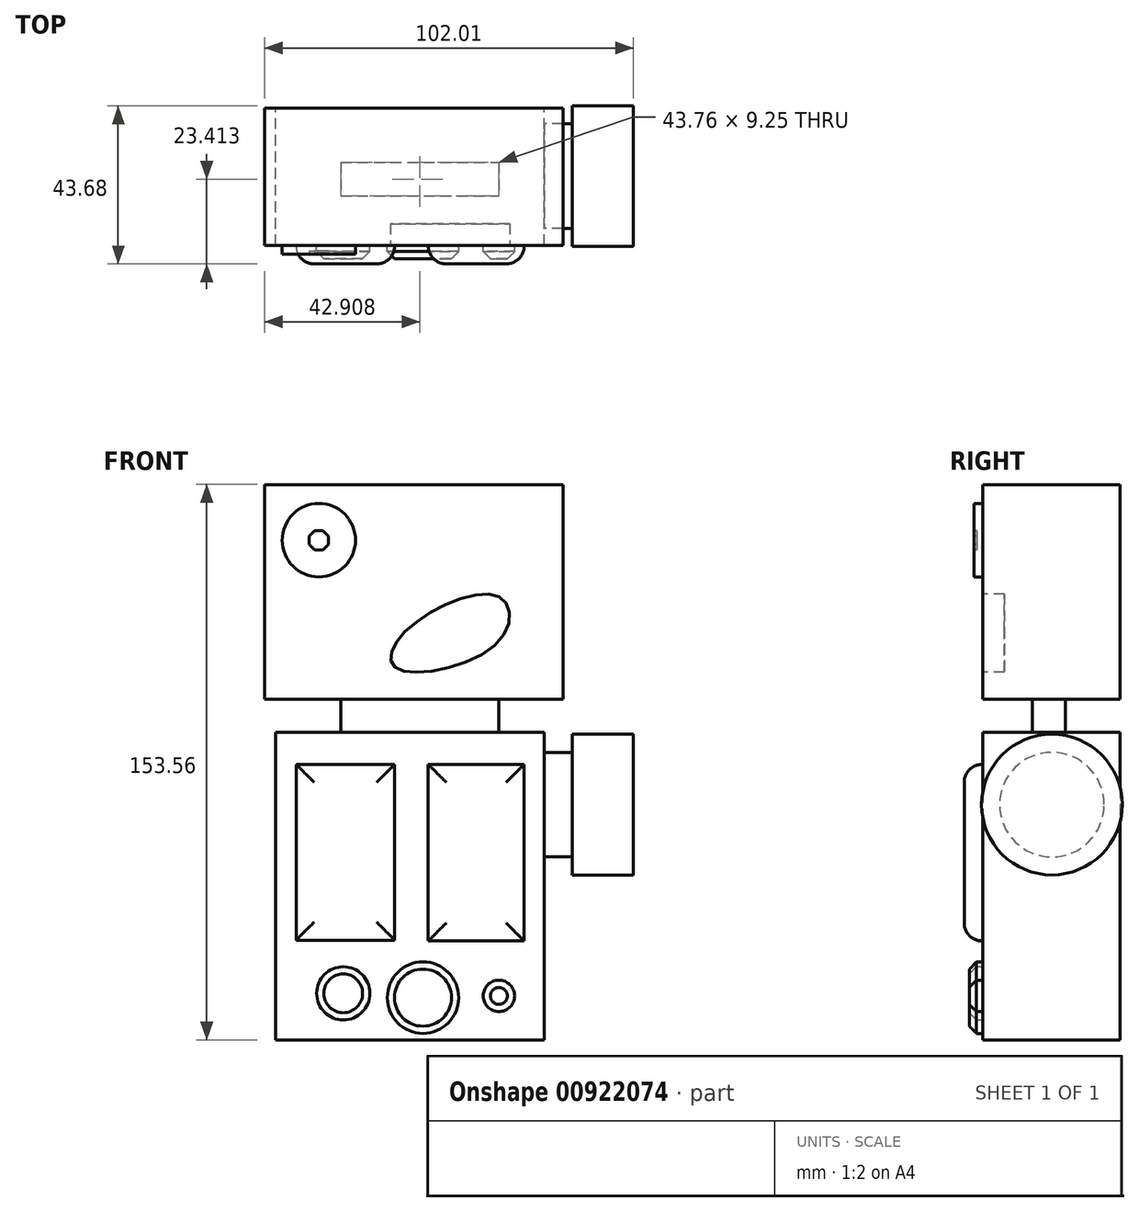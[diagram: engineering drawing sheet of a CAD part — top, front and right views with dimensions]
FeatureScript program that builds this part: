
annotation { "Feature Type Name" : "Feature", "Feature Type Description" : "" }
export const myFeature = defineFeature(function(context is Context, id is Id, definition is map)
    precondition{}
    {
        {
            var Q0;
            Q0=qCreatedBy(makeId("Front.planeOp"),FACE);
            var sketch = newSketch(context, id + "F0", { "sketchPlane" : qUnion([Q0])});
            skLineSegment(sketch, "E0.bottom", {"start": v(-61.73, 38.4) * mm, "end": v(12.52, 38.4) * mm});
            skLineSegment(sketch, "E0.top", {"start": v(-61.73, -46.66) * mm, "end": v(12.52, -46.66) * mm});
            skLineSegment(sketch, "E0.left", {"start": v(-61.73, 38.4) * mm, "end": v(-61.73, -46.66) * mm});
            skLineSegment(sketch, "E0.right", {"start": v(12.52, 38.4) * mm, "end": v(12.52, -46.66) * mm});
            skSolve(sketch);
        }
        {
            var Q0;
            Q0 = qSketchRegion(id + "F0", true);
            extrude(context, id + "F1", {"entities" : qUnion([Q0]), "depth" : 38 * mm, "offsetDistance" : 25 * mm});
        }
        {
            var Q0;
            Q0=makeQuery(id+"F1.opExtrude","CAP_FACE",FACE,{"disambiguationData":[OSD([sQuery(id+"F0.wireOp",EDGE,"E0.bottom"),sQuery(id+"F0.wireOp",EDGE,"E0.top"),sQuery(id+"F0.wireOp",EDGE,"E0.left"),sQuery(id+"F0.wireOp",EDGE,"E0.right")])],"isStart":false});
            var sketch = newSketch(context, id + "F2", { "sketchPlane" : qUnion([Q0])});
            skLineSegment(sketch, "E1.bottom", {"start": v(-56.1, 29.53) * mm, "end": v(-28.82, 29.53) * mm});
            skLineSegment(sketch, "E1.top", {"start": v(-56.1, -19.1) * mm, "end": v(-28.82, -19.1) * mm});
            skLineSegment(sketch, "E1.left", {"start": v(-56.1, 29.53) * mm, "end": v(-56.1, -19.1) * mm});
            skLineSegment(sketch, "E1.right", {"start": v(-28.82, 29.53) * mm, "end": v(-28.82, -19.1) * mm});
            skLineSegment(sketch, "E2.bottom", {"start": v(-19.57, 29.53) * mm, "end": v(7, 29.53) * mm});
            skLineSegment(sketch, "E2.top", {"start": v(-19.57, -19.33) * mm, "end": v(7, -19.33) * mm});
            skLineSegment(sketch, "E2.left", {"start": v(-19.57, 29.53) * mm, "end": v(-19.57, -19.33) * mm});
            skLineSegment(sketch, "E2.right", {"start": v(7, 29.53) * mm, "end": v(7, -19.33) * mm});
            skSolve(sketch);
        }
        {
            var Q0;
            Q0 = qSketchRegion(id + "F2", true);
            extrude(context, id + "F3", {"entities" : qUnion([Q0]), "operationType" : NewBodyOperationType.ADD, "depth" : 5.1 * mm, "offsetDistance" : 25 * mm});
        }
        {
            var Q0;
            Q0=makeQuery(id+"F3.opExtrude","CAP_EDGE",EDGE,{"disambiguationData":[OSD([sQuery(id+"F2.wireOp",EDGE,"E1.bottom")])],"isStart":false});
            var Q1;
            Q1=makeQuery(id+"F3.opExtrude","CAP_EDGE",EDGE,{"disambiguationData":[OSD([sQuery(id+"F2.wireOp",EDGE,"E2.bottom")])],"isStart":false});
            var Q2;
            Q2=makeQuery(id+"F3.opExtrude","CAP_EDGE",EDGE,{"disambiguationData":[OSD([sQuery(id+"F2.wireOp",EDGE,"E2.top")])],"isStart":false});
            var Q3;
            Q3=makeQuery(id+"F3.opExtrude","CAP_EDGE",EDGE,{"disambiguationData":[OSD([sQuery(id+"F2.wireOp",EDGE,"E1.top")])],"isStart":false});
            var Q4;
            Q4=makeQuery(id+"F3.opExtrude","CAP_EDGE",EDGE,{"disambiguationData":[OSD([sQuery(id+"F2.wireOp",EDGE,"E2.left")])],"isStart":false});
            var Q5;
            Q5=makeQuery(id+"F3.opExtrude","CAP_EDGE",EDGE,{"disambiguationData":[OSD([sQuery(id+"F2.wireOp",EDGE,"E1.right")])],"isStart":false});
            var Q6;
            Q6=makeQuery(id+"F3.opExtrude","CAP_EDGE",EDGE,{"disambiguationData":[OSD([sQuery(id+"F2.wireOp",EDGE,"E1.left")])],"isStart":false});
            var Q7;
            Q7=makeQuery(id+"F3.opExtrude","CAP_EDGE",EDGE,{"disambiguationData":[OSD([sQuery(id+"F2.wireOp",EDGE,"E2.right")])],"isStart":false});
            fillet(context, id + "F4", {"entities" : qUnion([Q0, Q1, Q2, Q3, Q4, Q5, Q6, Q7]), "radius" : 5 * mm, "tangentPropagation" : true, "allowEdgeOverflow" : false});
        }
        {
            var Q0;
            Q0=makeQuery(id+"F1.opExtrude","CAP_FACE",FACE,{"disambiguationData":[OSD([sQuery(id+"F0.wireOp",EDGE,"E0.bottom"),sQuery(id+"F0.wireOp",EDGE,"E0.top"),sQuery(id+"F0.wireOp",EDGE,"E0.left"),sQuery(id+"F0.wireOp",EDGE,"E0.right")])],"isStart":false});
            var sketch = newSketch(context, id + "F5", { "sketchPlane" : qUnion([Q0])});
            skCircle(sketch, "E3", {"center": v(-43.05, -33.8) * mm, "radius": 7.36 * mm});
            skCircle(sketch, "E4", {"center": v(-21, -34.99) * mm, "radius": 9.89 * mm});
            skCircle(sketch, "E5", {"center": v(0, -34.51) * mm, "radius": 4.35 * mm});
            skSolve(sketch);
        }
        {
            var Q0;
            Q0 = qSketchRegion(id + "F5", true);
            extrude(context, id + "F6", {"entities" : qUnion([Q0]), "operationType" : NewBodyOperationType.ADD, "depth" : 3.7 * mm, "offsetDistance" : 25 * mm});
        }
        {
            var Q0;
            Q0=makeQuery(id+"F6.opExtrude","CAP_EDGE",EDGE,{"disambiguationData":[OSD([sQuery(id+"F5.wireOp",EDGE,"E3")])],"isStart":false});
            var Q1;
            Q1=makeQuery(id+"F6.opExtrude","CAP_EDGE",EDGE,{"disambiguationData":[OSD([sQuery(id+"F5.wireOp",EDGE,"E4")])],"isStart":false});
            var Q2;
            Q2=makeQuery(id+"F6.opExtrude","CAP_EDGE",EDGE,{"disambiguationData":[OSD([sQuery(id+"F5.wireOp",EDGE,"E5")])],"isStart":false});
            chamfer(context, id + "F7", {"entities" : qUnion([Q0, Q1, Q2]), "width" : 2 * mm, "tangentPropagation" : true});
        }
        {
            var Q0;
            Q0=makeQuery(id+"F1.opExtrude","SWEPT_FACE",FACE,{"disambiguationData":[OSD([sQuery(id+"F0.wireOp",EDGE,"E0.right")])]});
            var sketch = newSketch(context, id + "F8", { "sketchPlane" : qUnion([Q0])});
            skCircle(sketch, "E6", {"center": v(-18.86, 18.38) * mm, "radius": 14.46 * mm});
            skSolve(sketch);
        }
        {
            var Q0;
            Q0 = qSketchRegion(id + "F8", true);
            extrude(context, id + "F9", {"entities" : qUnion([Q0]), "operationType" : NewBodyOperationType.ADD, "depth" : 7.8 * mm, "offsetDistance" : 25 * mm});
        }
        {
            var Q0;
            Q0=makeQuery(id+"F9.opExtrude","CAP_FACE",FACE,{"disambiguationData":[OSD([sQuery(id+"F8.wireOp",EDGE,"E6")])],"isStart":false});
            var sketch = newSketch(context, id + "F10", { "sketchPlane" : qUnion([Q0])});
            skCircle(sketch, "E7", {"center": v(-18.86, 18.38) * mm, "radius": 19.44 * mm});
            skSolve(sketch);
        }
        {
            var Q0;
            Q0 = qSketchRegion(id + "F10", true);
            extrude(context, id + "F11", {"entities" : qUnion([Q0]), "operationType" : NewBodyOperationType.ADD, "depth" : 16.9 * mm, "offsetDistance" : 25 * mm});
        }
        {
            var Q0;
            Q0=makeQuery(id+"F1.opExtrude","SWEPT_FACE",FACE,{"disambiguationData":[OSD([sQuery(id+"F0.wireOp",EDGE,"E0.bottom")])]});
            var sketch = newSketch(context, id + "F12", { "sketchPlane" : qUnion([Q0])});
            skLineSegment(sketch, "E8.bottom", {"start": v(-43.76, -15.06) * mm, "end": v(0, -15.06) * mm});
            skLineSegment(sketch, "E8.top", {"start": v(-43.76, -24.31) * mm, "end": v(0, -24.31) * mm});
            skLineSegment(sketch, "E8.left", {"start": v(-43.76, -15.06) * mm, "end": v(-43.76, -24.31) * mm});
            skLineSegment(sketch, "E8.right", {"start": v(0, -15.06) * mm, "end": v(0, -24.31) * mm});
            skSolve(sketch);
        }
        {
            var Q0;
            Q0 = qSketchRegion(id + "F12", true);
            extrude(context, id + "F13", {"entities" : qUnion([Q0]), "operationType" : NewBodyOperationType.ADD, "depth" : 9.1 * mm, "offsetDistance" : 25 * mm});
        }
        {
            var Q0;
            Q0=makeQuery(id+"F13.opExtrude","CAP_FACE",FACE,{"disambiguationData":[OSD([sQuery(id+"F12.wireOp",EDGE,"E8.bottom"),sQuery(id+"F12.wireOp",EDGE,"E8.top"),sQuery(id+"F12.wireOp",EDGE,"E8.left"),sQuery(id+"F12.wireOp",EDGE,"E8.right")])],"isStart":false});
            var sketch = newSketch(context, id + "F14", { "sketchPlane" : qUnion([Q0])});
            skLineSegment(sketch, "E9.bottom", {"start": v(-64.79, 0) * mm, "end": v(17.73, 0) * mm});
            skLineSegment(sketch, "E9.top", {"start": v(-64.79, -37.98) * mm, "end": v(17.73, -37.98) * mm});
            skLineSegment(sketch, "E9.left", {"start": v(-64.79, 0) * mm, "end": v(-64.79, -37.98) * mm});
            skLineSegment(sketch, "E9.right", {"start": v(17.73, 0) * mm, "end": v(17.73, -37.98) * mm});
            skSolve(sketch);
        }
        {
            var Q0;
            Q0 = qSketchRegion(id + "F14", true);
            extrude(context, id + "F15", {"entities" : qUnion([Q0]), "operationType" : NewBodyOperationType.ADD, "depth" : 59.4 * mm, "offsetDistance" : 25 * mm});
        }
        {
            var Q0;
            Q0=makeQuery(id+"F15.opExtrude","SWEPT_FACE",FACE,{"disambiguationData":[OSD([sQuery(id+"F14.wireOp",EDGE,"E9.top")])]});
            var sketch = newSketch(context, id + "F16", { "sketchPlane" : qUnion([Q0])});
            skFitSpline(sketch, "E10", {"points": [v(-26.03, 66.14) * mm, v(0, 75.92) * mm, v(0, 63.55) * mm, v(-28.33, 56.07) * mm, v(-26.03, 66.14) * mm]});
            skSolve(sketch);
        }
        {
            var Q0;
            Q0 = qSketchRegion(id + "F16", true);
            extrude(context, id + "F17", {"entities" : qUnion([Q0]), "operationType" : NewBodyOperationType.REMOVE, "oppositeDirection" : true, "depth" : 6 * mm, "offsetDistance" : 25 * mm});
        }
        {
            var Q0;
            Q0=makeQuery(id+"F15.opExtrude","SWEPT_FACE",FACE,{"disambiguationData":[OSD([sQuery(id+"F14.wireOp",EDGE,"E9.top")])]});
            var sketch = newSketch(context, id + "F18", { "sketchPlane" : qUnion([Q0])});
            skCircle(sketch, "E11", {"center": v(-49.8, 91.5) * mm, "radius": 10.15 * mm});
            skSolve(sketch);
        }
        {
            var Q0;
            Q0 = qSketchRegion(id + "F18", true);
            extrude(context, id + "F19", {"entities" : qUnion([Q0]), "operationType" : NewBodyOperationType.ADD, "depth" : 2.4 * mm, "offsetDistance" : 25 * mm});
        }
        {
            var Q0;
            Q0=makeQuery(id+"F19.opExtrude","CAP_FACE",FACE,{"disambiguationData":[OSD([sQuery(id+"F18.wireOp",EDGE,"E11")])],"isStart":false});
            var sketch = newSketch(context, id + "F20", { "sketchPlane" : qUnion([Q0])});
            skCircle(sketch, "E12.cCircle", {"center": v(-49.8, 91.5) * mm, "radius": 2.69 * mm, "construction": true});
            skLineSegment(sketch, "E12.0", {"start": v(-48.68, 88.81) * mm, "end": v(-50.91, 88.81) * mm});
            skLineSegment(sketch, "E12.1", {"start": v(-50.91, 88.81) * mm, "end": v(-52.48, 90.39) * mm});
            skLineSegment(sketch, "E12.2", {"start": v(-52.48, 90.39) * mm, "end": v(-52.48, 92.61) * mm});
            skLineSegment(sketch, "E12.3", {"start": v(-52.48, 92.61) * mm, "end": v(-50.91, 94.19) * mm});
            skLineSegment(sketch, "E12.4", {"start": v(-50.91, 94.19) * mm, "end": v(-48.68, 94.19) * mm});
            skLineSegment(sketch, "E12.5", {"start": v(-48.68, 94.19) * mm, "end": v(-47.11, 92.61) * mm});
            skLineSegment(sketch, "E12.6", {"start": v(-47.11, 92.61) * mm, "end": v(-47.11, 90.39) * mm});
            skLineSegment(sketch, "E12.7", {"start": v(-47.11, 90.39) * mm, "end": v(-48.68, 88.81) * mm});
            skPoint(sketch, "E12.0.midPoint", {"position": v(-49.8, 88.81) * mm});
            skSolve(sketch);
        }
        {
            var Q0;
            Q0 = qSketchRegion(id + "F20", true);
            extrude(context, id + "F21", {"entities" : qUnion([Q0]), "operationType" : NewBodyOperationType.REMOVE, "oppositeDirection" : true, "depth" : 0.8 * mm, "offsetDistance" : 25 * mm});
        }
    });
